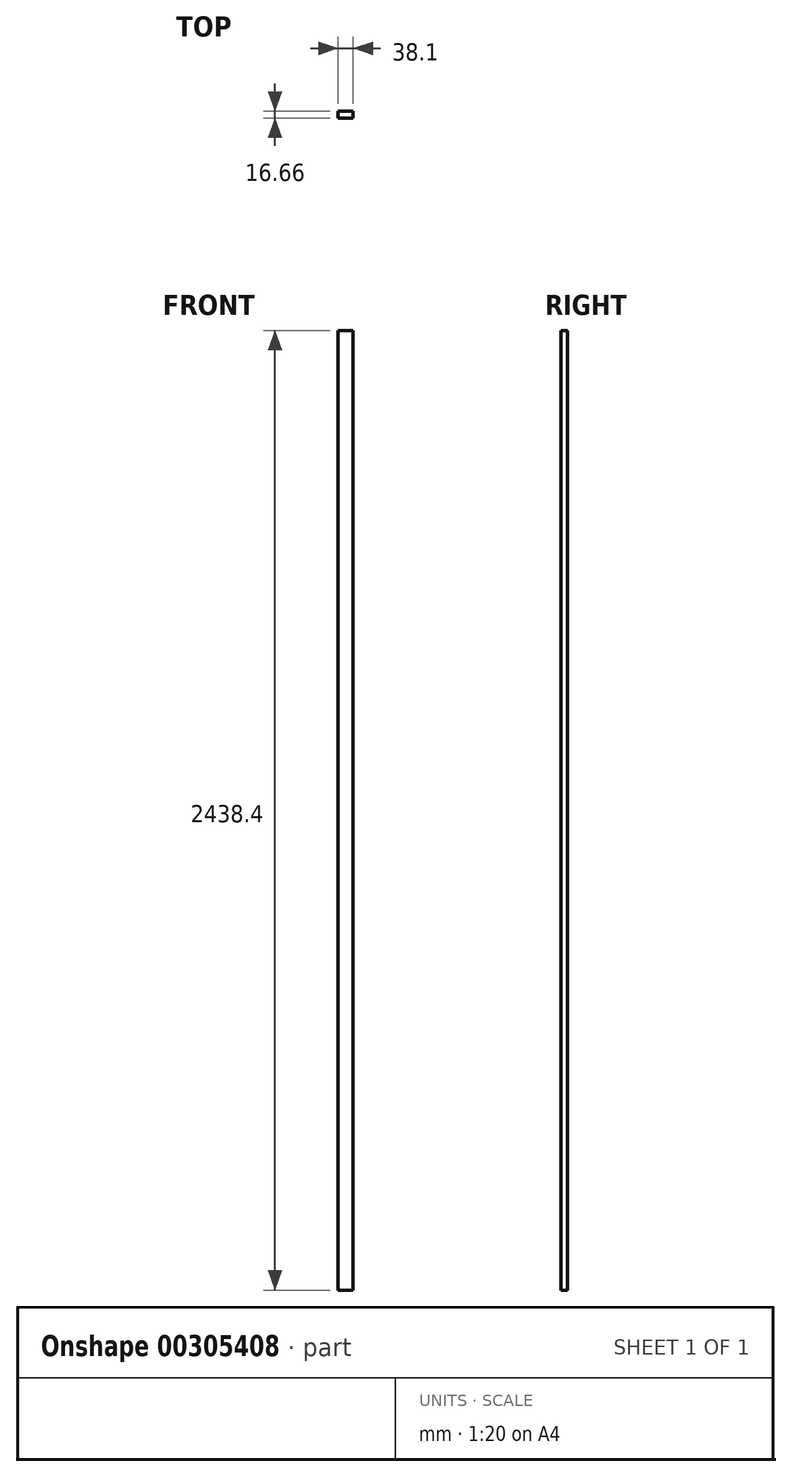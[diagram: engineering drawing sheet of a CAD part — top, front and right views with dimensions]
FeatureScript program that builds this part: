
annotation { "Feature Type Name" : "Feature", "Feature Type Description" : "" }
export const myFeature = defineFeature(function(context is Context, id is Id, definition is map)
    precondition{}
    {
        {
            var Q0;
            Q0=qCreatedBy(makeId("Front.planeOp"),FACE);
            var sketch = newSketch(context, id + "F0", { "sketchPlane" : qUnion([Q0])});
            skLineSegment(sketch, "E0.bottom", {"start": v(-21.83, 2329.03) * mm, "end": v(16.27, 2329.03) * mm});
            skLineSegment(sketch, "E0.top", {"start": v(-21.83, -109.37) * mm, "end": v(16.27, -109.37) * mm});
            skLineSegment(sketch, "E0.left", {"start": v(-21.83, 2329.03) * mm, "end": v(-21.83, -109.37) * mm});
            skLineSegment(sketch, "E0.right", {"start": v(16.27, 2329.03) * mm, "end": v(16.27, -109.37) * mm});
            skSolve(sketch);
        }
        {
            var Q0;
            Q0=makeQuery(id+"F0.imprint","IMPRINT",FACE,{"disambiguationData":[TD([[makeQuery(id+"F0.imprint","IMPRINT",EDGE,{"derivedFrom":sQuery(id+"F0.wireOp",EDGE,"E0.bottom")}),-1.0]])]});
            extrude(context, id + "F1", {"entities" : qUnion([Q0]), "depth" : 16.66 * mm});
        }
    });
